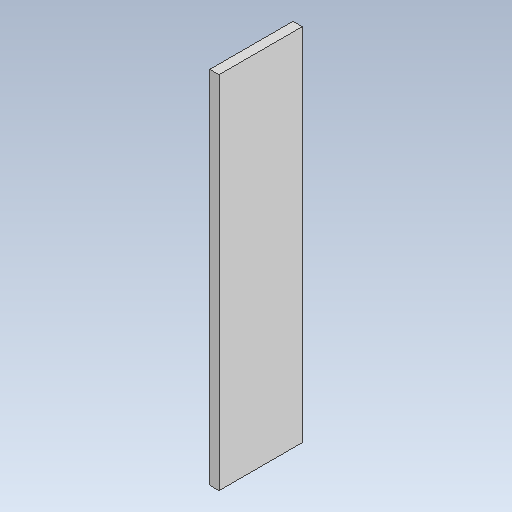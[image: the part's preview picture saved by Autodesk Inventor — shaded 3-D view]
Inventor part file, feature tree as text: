
AUTODESK INVENTOR PART (.ipt)
format: ipt  version: 2021 (Build 250183000, 183)  size: 77,824 bytes
history: native  units: mm
features: extrude x1, sketch x1
ambient origin geometry x8: Origin, YZ Plane, XZ Plane, XY Plane, X Axis, Y Axis, Z Axis, Center Point
bodies: Solid1 (feature_tree)
feature tree (2):
  extrude  "Extrusion1"  Depth=180.0mm
  sketch  "Sketch1"  dims[d0=780.0mm d1=180.0mm d2=20.0mm d3=0.0mm]
